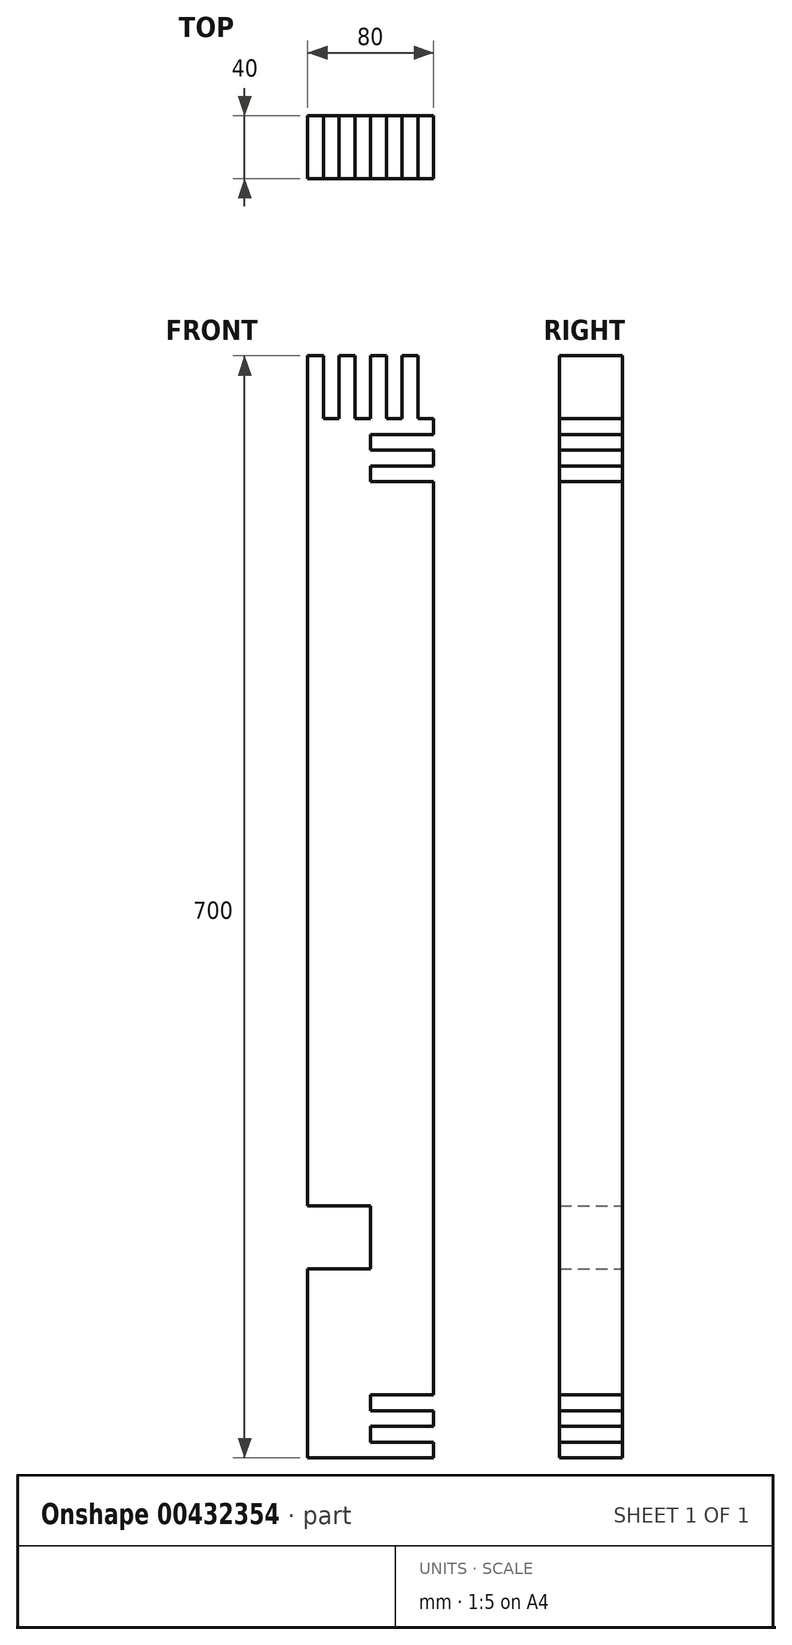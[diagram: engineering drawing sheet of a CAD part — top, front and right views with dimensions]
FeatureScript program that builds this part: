
annotation { "Feature Type Name" : "Feature", "Feature Type Description" : "" }
export const myFeature = defineFeature(function(context is Context, id is Id, definition is map)
    precondition{}
    {
        {
            var Q0;
            Q0=qCreatedBy(makeId("Front.planeOp"),FACE);
            var sketch = newSketch(context, id + "F0", { "sketchPlane" : qUnion([Q0])});
            skLineSegment(sketch, "E0", {"start": v(-49.91, 600.4) * mm, "end": v(-40, 600.4) * mm});
            skLineSegment(sketch, "E1", {"start": v(-40, 600.4) * mm, "end": v(-40, 560.4) * mm});
            skLineSegment(sketch, "E2", {"start": v(-40, 560.4) * mm, "end": v(-30, 560.4) * mm});
            skLineSegment(sketch, "E3", {"start": v(-30, 560.4) * mm, "end": v(-30, 600.4) * mm});
            skLineSegment(sketch, "E4", {"start": v(-30, 600.4) * mm, "end": v(-20, 600.4) * mm});
            skLineSegment(sketch, "E5", {"start": v(-20, 600.4) * mm, "end": v(-20, 560.4) * mm});
            skLineSegment(sketch, "E6", {"start": v(-20, 560.4) * mm, "end": v(-10, 560.4) * mm});
            skLineSegment(sketch, "E7", {"start": v(-10, 560.4) * mm, "end": v(-10, 600.4) * mm});
            skLineSegment(sketch, "E8", {"start": v(-10, 600.4) * mm, "end": v(0, 600.4) * mm});
            skLineSegment(sketch, "E9", {"start": v(0, 600.4) * mm, "end": v(0, 560.4) * mm});
            skLineSegment(sketch, "E10", {"start": v(0, 560.4) * mm, "end": v(10, 560.4) * mm});
            skLineSegment(sketch, "E11", {"start": v(10, 560.4) * mm, "end": v(10, 600.4) * mm});
            skLineSegment(sketch, "E12", {"start": v(10, 600.4) * mm, "end": v(20, 600.4) * mm});
            skLineSegment(sketch, "E13", {"start": v(20, 600.4) * mm, "end": v(20, 560.4) * mm});
            skLineSegment(sketch, "E14", {"start": v(20, 560.4) * mm, "end": v(30, 560.4) * mm});
            skLineSegment(sketch, "E15", {"start": v(30, 560.4) * mm, "end": v(30, 550.4) * mm});
            skLineSegment(sketch, "E16", {"start": v(-10, 550.4) * mm, "end": v(-10, 540.4) * mm});
            skLineSegment(sketch, "E17", {"start": v(-10, 540.4) * mm, "end": v(30, 540.4) * mm});
            skLineSegment(sketch, "E18", {"start": v(30, 540.4) * mm, "end": v(30, 530.4) * mm});
            skLineSegment(sketch, "E19", {"start": v(30, 530.4) * mm, "end": v(-10, 530.4) * mm});
            skLineSegment(sketch, "E20", {"start": v(-10, 530.4) * mm, "end": v(-10, 520.4) * mm});
            skLineSegment(sketch, "E21", {"start": v(-10, 520.4) * mm, "end": v(30, 520.4) * mm});
            skLineSegment(sketch, "E22", {"start": v(-10, 550.4) * mm, "end": v(30, 550.4) * mm});
            skLineSegment(sketch, "E23", {"start": v(-49.91, 20.4) * mm, "end": v(-9.91, 20.4) * mm});
            skLineSegment(sketch, "E24", {"start": v(-9.91, 20.4) * mm, "end": v(-9.91, 60.4) * mm});
            skLineSegment(sketch, "E25", {"start": v(-9.91, 60.4) * mm, "end": v(-49.91, 60.4) * mm});
            skLineSegment(sketch, "E26", {"start": v(-49.91, 20.4) * mm, "end": v(-49.91, -99.6) * mm});
            skLineSegment(sketch, "E27", {"start": v(-49.91, 60.4) * mm, "end": v(-49.91, 600.4) * mm});
            skLineSegment(sketch, "E28", {"start": v(30.09, -59.6) * mm, "end": v(30, 520.4) * mm});
            skLineSegment(sketch, "E29", {"start": v(-49.91, -99.6) * mm, "end": v(30.09, -99.6) * mm});
            skLineSegment(sketch, "E30", {"start": v(30.09, -99.6) * mm, "end": v(30.09, -89.6) * mm});
            skLineSegment(sketch, "E31", {"start": v(30.09, -79.6) * mm, "end": v(30.09, -69.6) * mm});
            skLineSegment(sketch, "E32", {"start": v(30.09, -89.6) * mm, "end": v(-9.91, -89.6) * mm});
            skLineSegment(sketch, "E33", {"start": v(-9.91, -89.6) * mm, "end": v(-9.91, -79.6) * mm});
            skLineSegment(sketch, "E34", {"start": v(-9.91, -79.6) * mm, "end": v(30.09, -79.6) * mm});
            skLineSegment(sketch, "E35", {"start": v(30.09, -69.6) * mm, "end": v(-9.91, -69.6) * mm});
            skLineSegment(sketch, "E36", {"start": v(-9.91, -69.6) * mm, "end": v(-9.91, -59.6) * mm});
            skLineSegment(sketch, "E37", {"start": v(-9.91, -59.6) * mm, "end": v(30.09, -59.6) * mm});
            skSolve(sketch);
        }
        {
            var Q0;
            Q0=makeQuery(id+"F0.imprint","IMPRINT",FACE,{"disambiguationData":[TD([[makeQuery(id+"F0.imprint","IMPRINT",EDGE,{"derivedFrom":sQuery(id+"F0.wireOp",EDGE,"E0")}),-1.0]])]});
            extrude(context, id + "F1", {"entities" : qUnion([Q0]), "endBound" : BoundingType.SYMMETRIC, "depth" : 40 * mm});
        }
    });
